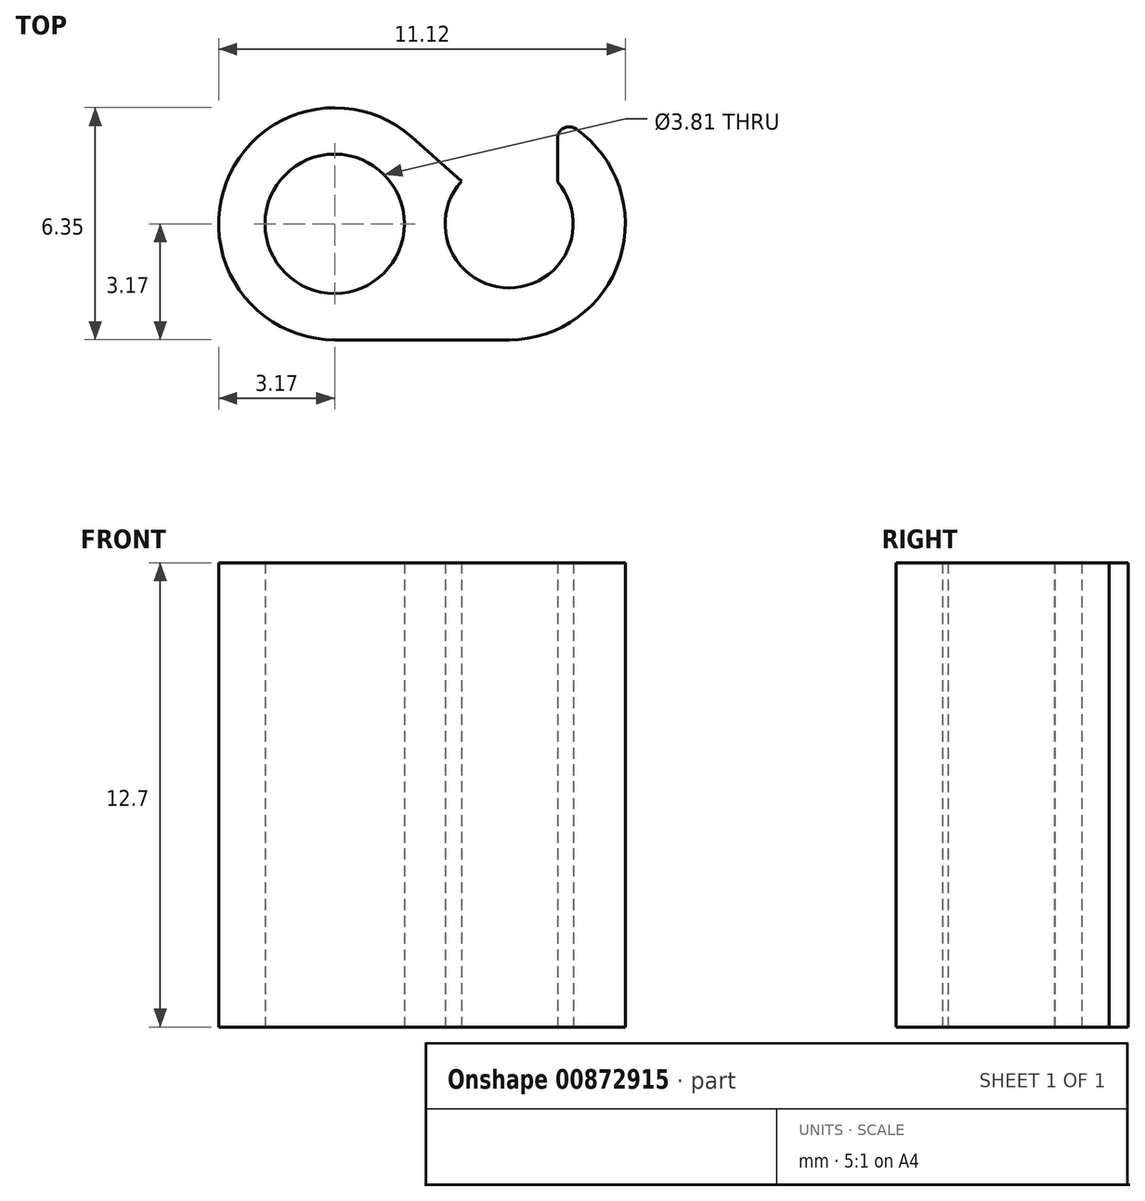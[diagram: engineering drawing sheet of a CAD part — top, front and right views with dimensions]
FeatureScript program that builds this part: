
annotation { "Feature Type Name" : "Feature", "Feature Type Description" : "" }
export const myFeature = defineFeature(function(context is Context, id is Id, definition is map)
    precondition{}
    {
        {
            var Q0;
            Q0=qCreatedBy(makeId("Top.planeOp"),FACE);
            var sketch = newSketch(context, id + "F0", { "sketchPlane" : qUnion([Q0])});
            skCircle(sketch, "E0", {"center": v(0, 0) * mm, "radius": 1.9 * mm});
            skArc(sketch, "E1", {"start": v(2.11, 2.37) * mm, "mid": v(-2.97, 1.13) * mm, "end": v(0, -3.18) * mm});
            skArc(sketch, "E2", {"start": v(3.47, 1.17) * mm, "mid": v(4.77, -1.75) * mm, "end": v(6.1, 1.15) * mm});
            skPoint(sketch, "E3.visualSharp", {"position": v(3.18, 0) * mm});
            skArc(sketch, "E4", {"start": v(4.78, -3.18) * mm, "mid": v(7.8, -0.96) * mm, "end": v(6.6, 2.6) * mm});
            skLineSegment(sketch, "E5", {"start": v(2.11, 2.37) * mm, "end": v(3.47, 1.17) * mm});
            skLineSegment(sketch, "E6", {"start": v(3.45, 2.89) * mm, "end": v(3.45, 1.15) * mm, "construction": true});
            skPoint(sketch, "E6.startSnap0", {"position": v(3.45, 1.19) * mm});
            skLineSegment(sketch, "E7", {"start": v(4.78, 0) * mm, "end": v(4.78, 3.35) * mm, "construction": true});
            skPoint(sketch, "E8.orphan", {"position": v(3.45, 4.6) * mm});
            skLineSegment(sketch, "E9.MirrorCS", {"start": v(6.1, 2.33) * mm, "end": v(6.1, 1.15) * mm});
            skLineSegment(sketch, "E10", {"start": v(0, -3.18) * mm, "end": v(4.78, -3.18) * mm});
            skArc(sketch, "E11", {"start": v(6.6, 2.6) * mm, "mid": v(6.27, 2.62) * mm, "end": v(6.1, 2.33) * mm});
            skPoint(sketch, "E12.orphan", {"position": v(6.1, 2.89) * mm});
            skSolve(sketch);
        }
        {
            var Q0;
            Q0 = qSketchRegion(id + "F0", true);
            extrude(context, id + "F1", {"entities" : qUnion([Q0]), "depth" : 12.7 * mm, "offsetDistance" : 25.4 * mm});
        }
    });
